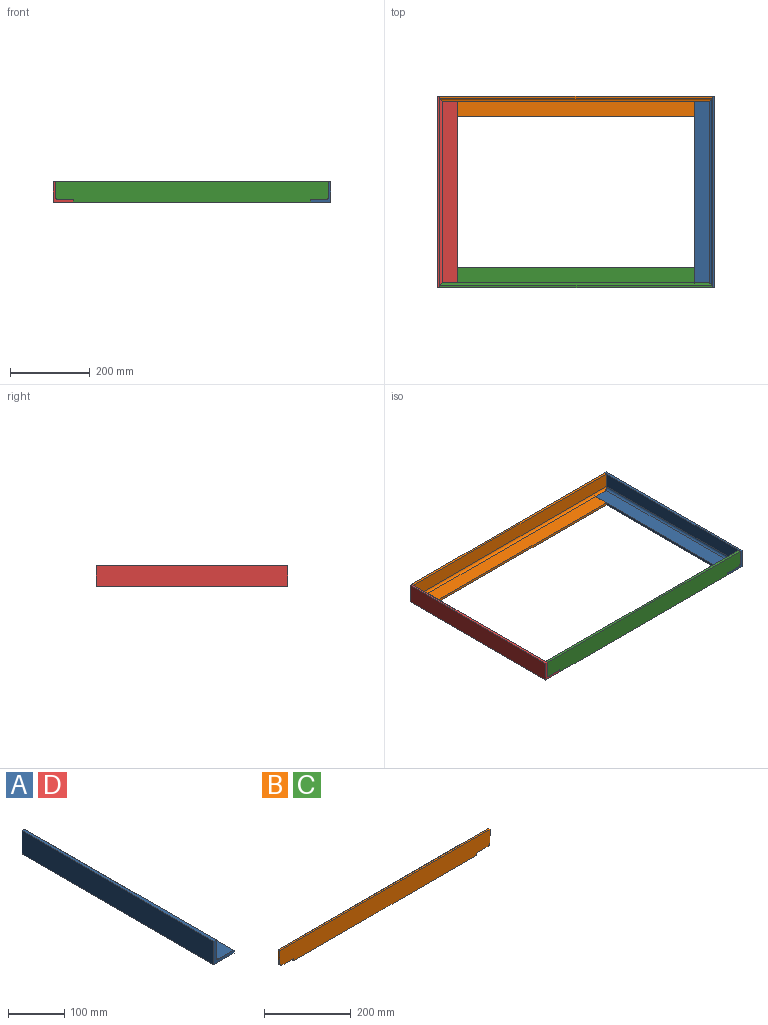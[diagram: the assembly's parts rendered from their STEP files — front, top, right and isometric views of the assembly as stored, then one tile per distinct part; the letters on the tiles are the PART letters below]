
ASSEMBLY  parts=4 mates=9
PART A: 9 faces, bbox 50.8x482.6x50.8 mm
  f0: plane 482.6x50.8mm, normal (-1,0,0), area 24516.1mm2, adj f1,f6,f7,f8
  f1: plane 482.6x50.8mm, normal (0,0,-1), area 24516.1mm2, adj f0,f2,f7,f8
  f2: plane 482.6x6.35mm, normal (1,0,0), area 3064.5mm2, adj f1,f3,f7,f8
  f3: plane 482.6x38.1mm, normal (0,0,1), area 18387.1mm2, adj f2,f4,f7,f8
  f4: cylinder r=6.35mm len=482.6mm, axis (0,1,0), area 4813.7mm2, adj f3,f5,f7,f8
  f5: plane 482.6x38.1mm, normal (1,0,0), area 18387.1mm2, adj f4,f6,f7,f8
  f6: plane 482.6x6.35mm, normal (0,0,1), area 3064.5mm2, adj f0,f5,f7,f8
  f7: plane 50.8x50.8mm, normal (0,-1,0), area 613.5mm2, adj f0,f1,f2,f3,f4,f5,f6
  f8: plane 50.8x50.8mm, normal (0,1,0), area 613.5mm2, adj f0,f1,f2,f3,f4,f5,f6
PART B: 15 faces, bbox 685.8x50.8x50.8 mm
  f0: plane 685.8x50.8mm, normal (0,-1,0), area 34256.8mm2, adj f1,f4,f5,f8,f9,f10,f11,f12
  f1: plane 596.9x50.8mm, normal (0,0,-1), area 30322.5mm2, adj f0,f2,f9,f11
  f2: plane 596.9x6.35mm, normal (0,1,0), area 3790.3mm2, adj f1,f3,f9,f11
  f3: plane 596.9x38.1mm, normal (0,0,1), area 22741.9mm2, adj f2,f6,f9,f11
  f4: plane 38.1x6.35mm, normal (1,0,0), area 241.9mm2, adj f0,f7,f8,f13
  f5: plane 38.1x6.35mm, normal (-1,0,0), area 241.9mm2, adj f0,f7,f8,f14
  f6: cylinder r=6.35mm len=685.8mm, axis (-1,0,0), area 6794.5mm2, adj f3,f7,f10,f12,f13,f14
  f7: plane 685.8x38.1mm, normal (0,1,0), area 26129mm2, adj f4,f5,f6,f8
  f8: plane 685.8x6.35mm, normal (0,0,1), area 4354.8mm2, adj f0,f4,f5,f7
  f9: plane 50.8x6.35mm, normal (-1,0,0), area 322.6mm2, adj f0,f1,f2,f3,f10
  f10: plane 38.1x12.7mm, normal (0,0,-1), area 483.9mm2, adj f0,f6,f9,f14
  f11: plane 50.8x6.35mm, normal (1,0,0), area 322.6mm2, adj f0,f1,f2,f3,f12
  f12: plane 38.1x12.7mm, normal (0,0,-1), area 483.9mm2, adj f0,f6,f11,f13
  f13: cylinder r=6.35mm len=12.7mm, axis (0,1,0), area 86.4mm2, adj f0,f4,f6,f12
  f14: cylinder r=6.35mm len=12.7mm, axis (0,-1,0), area 86.4mm2, adj f0,f5,f6,f10
PART C: same geometry as B
PART D: same geometry as A
PLACE A rot(axis=(0,-1,0),90deg) t=(76.93,460.53,-26.38)mm
PLACE B rot(axis=(0,0,1),180deg) t=(70.58,460.53,-26.38)mm
PLACE C t=(-615.22,-22.07,-26.38)mm
PLACE D t=(-621.57,460.53,-26.38)mm
MATE planar C.f12 <-> A.f5  axis (0,0,-1) through (45.18,-15.72,-20.03)mm
MATE planar C.f4 <-> A.f3  axis (1,0,0) through (70.58,-18.9,5.37)mm
MATE planar D.f7 <-> C.f0  axis (0,-1,0) through (-615.22,-22.07,-13.68)mm
MATE planar D.f5 <-> C.f5  axis (1,0,0) through (-615.22,219.23,5.37)mm
MATE planar A.f0 <-> B.f1  axis (0,0,-1) through (51.53,219.23,-26.38)mm
MATE planar B.f0 <-> A.f8  axis (0,1,0) through (-272.32,460.53,-0.61)mm
MATE planar C.f0 <-> A.f7  axis (0,-1,0) through (-272.32,-22.07,-0.61)mm
MATE planar B.f5 <-> A.f3  axis (1,0,0) through (70.58,457.35,5.37)mm
MATE planar D.f1 <-> A.f0  axis (0,0,-1) through (-596.17,-22.07,-26.38)mm
